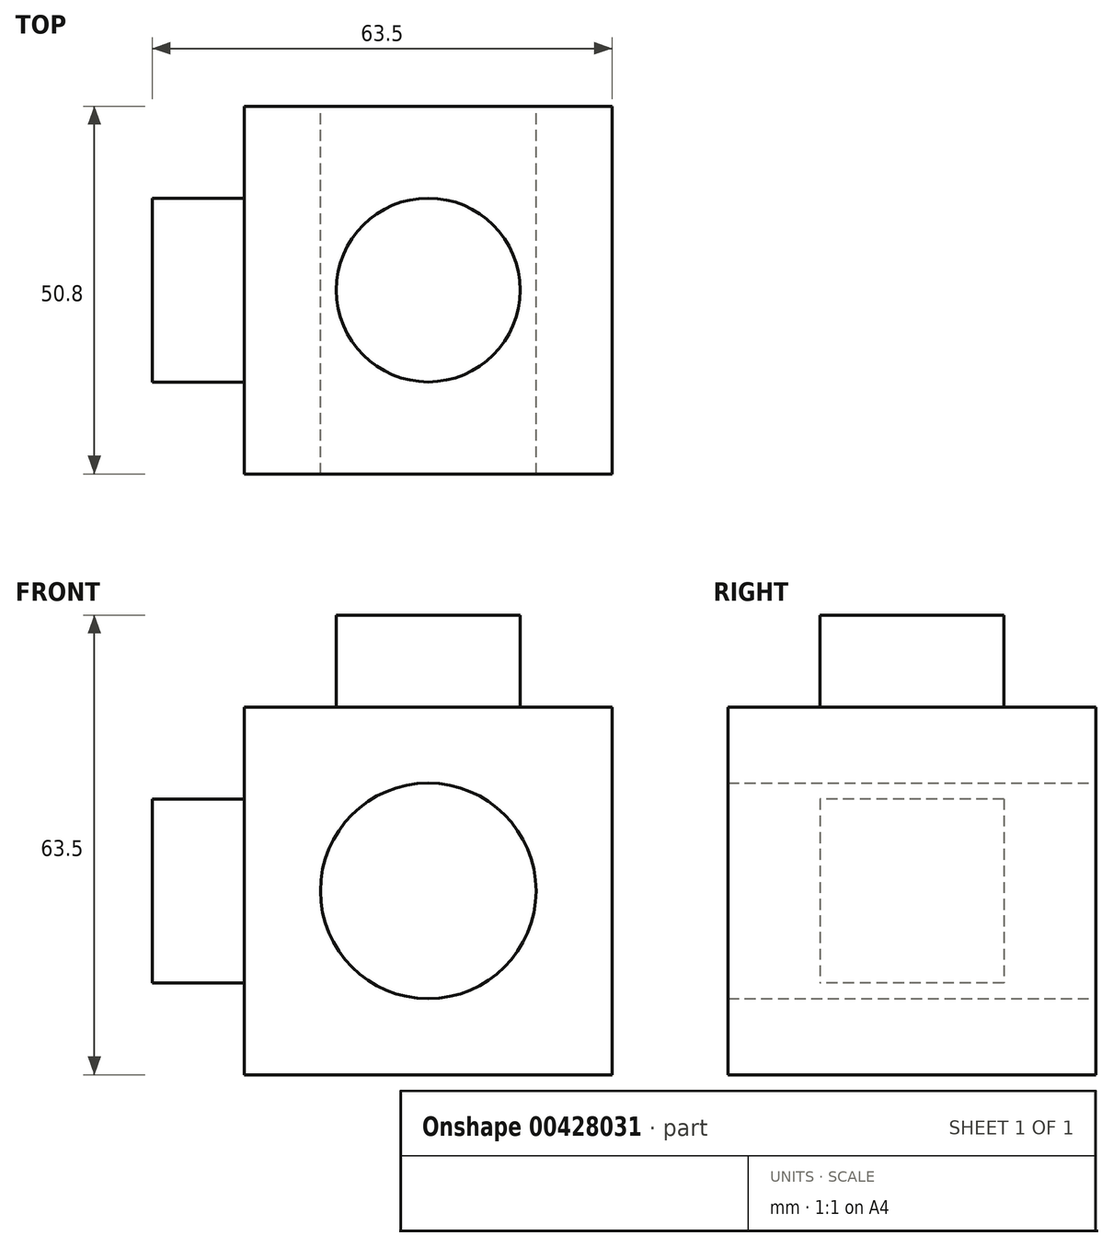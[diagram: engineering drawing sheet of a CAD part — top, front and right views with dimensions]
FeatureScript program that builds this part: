
annotation { "Feature Type Name" : "Feature", "Feature Type Description" : "" }
export const myFeature = defineFeature(function(context is Context, id is Id, definition is map)
    precondition{}
    {
        {
            var Q0;
            Q0=qCreatedBy(makeId("Front.planeOp"),FACE);
            var sketch = newSketch(context, id + "F0", { "sketchPlane" : qUnion([Q0])});
            skLineSegment(sketch, "E0.bottom", {"start": v(0, 0) * mm, "end": v(-50.8, 0) * mm});
            skLineSegment(sketch, "E0.top", {"start": v(0, -50.8) * mm, "end": v(-50.8, -50.8) * mm});
            skLineSegment(sketch, "E0.left", {"start": v(0, 0) * mm, "end": v(0, -50.8) * mm});
            skLineSegment(sketch, "E0.right", {"start": v(-50.8, 0) * mm, "end": v(-50.8, -50.8) * mm});
            skCircle(sketch, "E1", {"center": v(-25.4, -25.4) * mm, "radius": 14.89 * mm});
            skSolve(sketch);
        }
        {
            var Q0;
            Q0 = qSketchRegion(id + "F0", true);
            extrude(context, id + "F1", {"entities" : qUnion([Q0]), "depth" : 50.8 * mm});
        }
        {
            var Q0;
            Q0=makeQuery(id+"F1.opExtrude","SWEPT_FACE",FACE,{"disambiguationData":[OSD([sQuery(id+"F0.wireOp",EDGE,"E0.right")])]});
            var sketch = newSketch(context, id + "F2", { "sketchPlane" : qUnion([Q0])});
            skLineSegment(sketch, "E2.bottom", {"start": v(12.7, -12.7) * mm, "end": v(38.1, -12.7) * mm});
            skLineSegment(sketch, "E2.top", {"start": v(12.7, -38.1) * mm, "end": v(38.1, -38.1) * mm});
            skLineSegment(sketch, "E2.left", {"start": v(12.7, -12.7) * mm, "end": v(12.7, -38.1) * mm});
            skLineSegment(sketch, "E2.right", {"start": v(38.1, -12.7) * mm, "end": v(38.1, -38.1) * mm});
            skSolve(sketch);
        }
        {
            var Q0;
            Q0=makeQuery(id+"F2.imprint","IMPRINT",FACE,{"disambiguationData":[TD([[makeQuery(id+"F2.imprint","IMPRINT",EDGE,{"derivedFrom":sQuery(id+"F2.wireOp",EDGE,"E2.bottom")}),-1.0]])]});
            extrude(context, id + "F3", {"entities" : qUnion([Q0]), "operationType" : NewBodyOperationType.ADD, "depth" : 12.7 * mm});
        }
        {
            var Q0;
            Q0=makeQuery(id+"F1.opExtrude","SWEPT_FACE",FACE,{"disambiguationData":[OSD([sQuery(id+"F0.wireOp",EDGE,"E0.bottom")])]});
            var sketch = newSketch(context, id + "F4", { "sketchPlane" : qUnion([Q0])});
            skCircle(sketch, "E3", {"center": v(-25.4, -25.4) * mm, "radius": 12.7 * mm});
            skSolve(sketch);
        }
        {
            var Q0;
            Q0=makeQuery(id+"F4.imprint","IMPRINT",FACE,{"disambiguationData":[TD([[makeQuery(id+"F4.imprint","IMPRINT",EDGE,{"derivedFrom":sQuery(id+"F4.wireOp",EDGE,"E3")}),1.0]])]});
            extrude(context, id + "F5", {"entities" : qUnion([Q0]), "operationType" : NewBodyOperationType.ADD, "depth" : 12.7 * mm});
        }
    });
